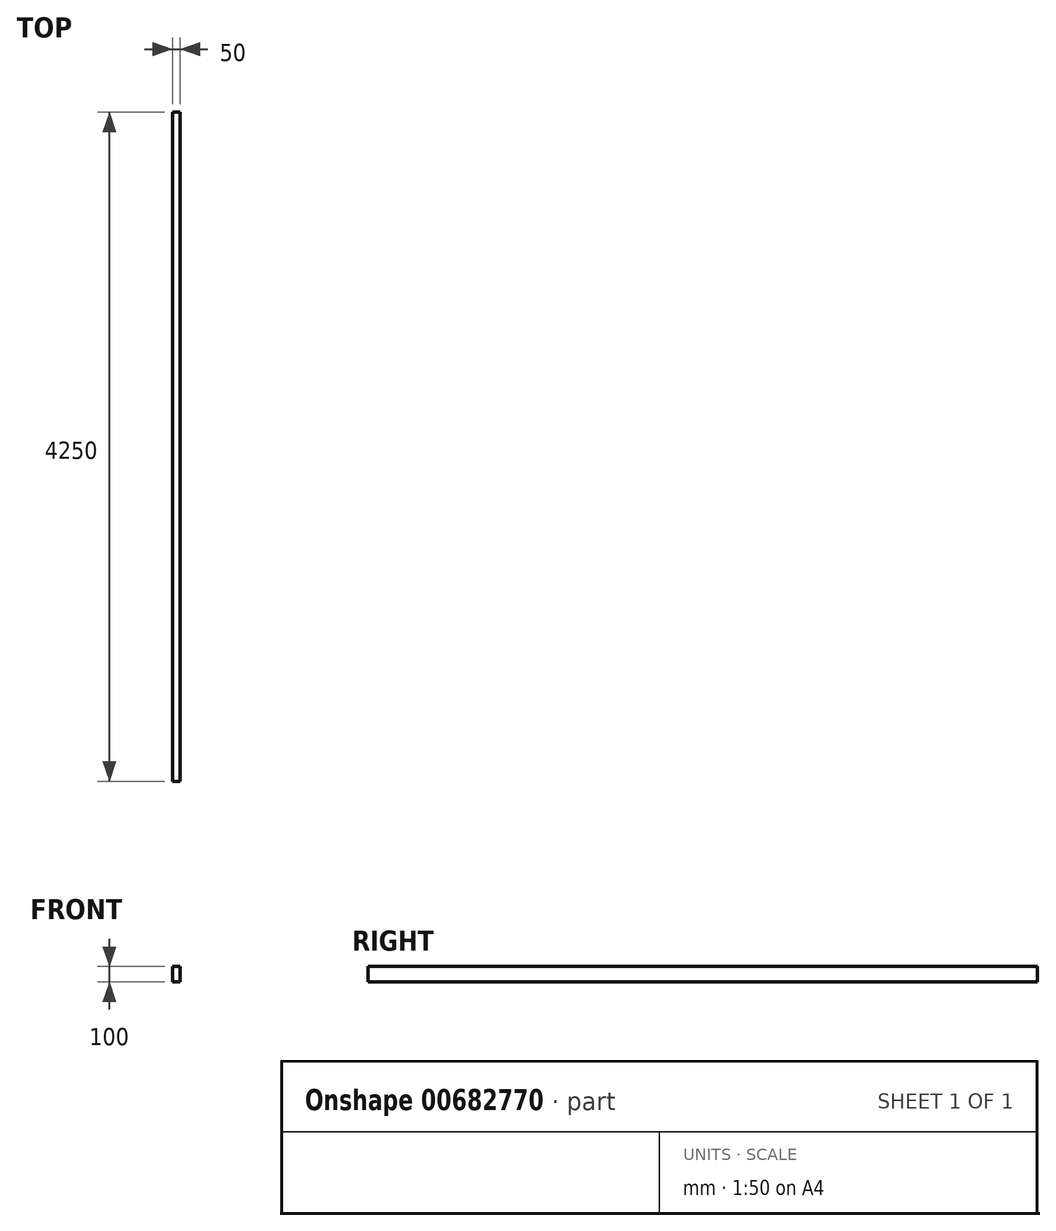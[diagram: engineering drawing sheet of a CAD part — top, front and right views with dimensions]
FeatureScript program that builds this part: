
annotation { "Feature Type Name" : "Feature", "Feature Type Description" : "" }
export const myFeature = defineFeature(function(context is Context, id is Id, definition is map)
    precondition{}
    {
        {
            var Q0;
            Q0=qCreatedBy(makeId("Front.planeOp"),FACE);
            var sketch = newSketch(context, id + "F0", { "sketchPlane" : qUnion([Q0])});
            skLineSegment(sketch, "E0.bottom", {"start": v(-85.58, 116.4) * mm, "end": v(-35.58, 116.4) * mm});
            skLineSegment(sketch, "E0.top", {"start": v(-85.58, 16.4) * mm, "end": v(-35.58, 16.4) * mm});
            skLineSegment(sketch, "E0.left", {"start": v(-85.58, 116.4) * mm, "end": v(-85.58, 16.4) * mm});
            skLineSegment(sketch, "E0.right", {"start": v(-35.58, 116.4) * mm, "end": v(-35.58, 16.4) * mm});
            skSolve(sketch);
        }
        {
            var Q0;
            Q0 = qSketchRegion(id + "F0", true);
            extrude(context, id + "F1", {"entities" : qUnion([Q0]), "depth" : 4250 * mm, "offsetDistance" : 25 * mm});
        }
    });
